# Revit family: done-2015_Valvula_Valvulas-Arco_Tajo-Pro-Bridas
name_source: partatom
category: Pipe Accessories
revit_build: Autodesk Revit 2015 (Build: 20140223_1515(x64)
units: mm (PartAtom-declared; Revit-internal decimal feet)

## types (2) — shared parameters
Acabado = Cromado
Autor = Bimetica PDS
COBieCategoria = IfcValve
Clase Brida = PN16
ClasificacionDeCierre = 0.00 bar
Codigo = 3
CodigoGubimclass = 50.10.20.10
CoeficienteDeCaudal = 418
Cost = 0.00€
DescripcionGubimclass = Válvulas e instrumentos de medida y control de flujo de fontanería
Description = Válvula esfera doble eje TAJO PRO doble mando conexión embridada
Diam. Agujeros = 18.000 mm
FechaEmisionElementoBIM = 11/02/2020
FechaVencimientoElementoBIM = 11/02/2021
GarantiaExtendida = Yes
Historial = (RVT2015-V01) Creación del elemento
IfcExportAs = IfcValve
IfcExportType = Ball Valve
K Coefficient = 0.35
Manufacturer = Vávulas Arco S.L
Marcado CE = Yes
MasterformatCodigo = 35 20 19
MasterformatTitulo = Hydraulic Valves
MaterialCarcasa = Latón Europeo CW617N
MecanismoValvula = BALL
Model = TAJO PRO BRIDAS
No. Agujeros = 8
Numero de Licencia = XXX-XXXX9536
OmniclassCodigo = 23-27 31 15
OmniclassTitulo = Ball Valves
OperacionValvula = PALANCA
PatronValvula = STRAIGHT_2_PORT
PresionDePrueba = 0.00 bar
PresionDeTrabajo = 0.00 bar
PresionNominal = 16.00 bar
Radio Agujero = 9.000 mm
Referencia = 3
Sistema = Agua potable y agua caliente sanitaria
TelefonoContacto = 0034 963 17 10 70
TemperaturaMaxima = 140 °C
TemprerturaMinima = -20 °C
Titular = Vávulas Arco S.L
Type Comments = Agua potable y agua caliente sanitaria
UNSPSCCodigo = 40141607
UNSPSCTitulo = Ball valves
URLPerfilProductoBimetica = https://bimetica.com
Uniclass2015Codigo = 65-54-95-13
Uniclass2015Titulo = Check valves
Version = RVT2015
zero-valued in all types: AcidificacionAtmosfericaPorUnidad, AguaConsumidaPorUnidad, CambioClimaticoPorUnidad, CosteMantenimiento, CurvaSonido, DestruccionCapaOzonoEstratosfericaPorUnidad, Energia consumida, EnergiaNoRenovableConsumidaPorUnidad, EnergiaPrimariaTotalConsumidaPorUnidad, EnergiaRenovableConsumidaPorUnidad, EutrofizacionPorUnidad, FaltaDeRecursosPorUnidad, FechaEvaluacion, FormacionFotoquimicaOzonoPorUnidad, ResiduoInertePorUnidad, ResiduoRadioactivoPorUnidad, ResiduosNoPeligrososPorUnidad, ResiduosPeligrososPorUnidad

## per-type parameters (varying)
| type | A | B di | C | D | D di | F | Longitud | R | Radio A | Radio D | Radio Nominal | Tamano |
| 3 | 122.000 mm | 247.000 mm | 152.000 mm | 200.000 mm | 246.000 mm | 18.000 mm | 118.000 mm | 2" | 48.800 mm | 100.000 mm | 85.000 mm | 5" |
| 4 | 141.000 mm | 262.000 mm | 170.000 mm | 220.000 mm | 266.000 mm | 20.000 mm | 137.000 mm | 3" | 56.400 mm | 110.000 mm | 95.000 mm | 6" |

## geometry (parser evidence)
native form markers: Sweep x2
no freeform markers — native parametric forms only
